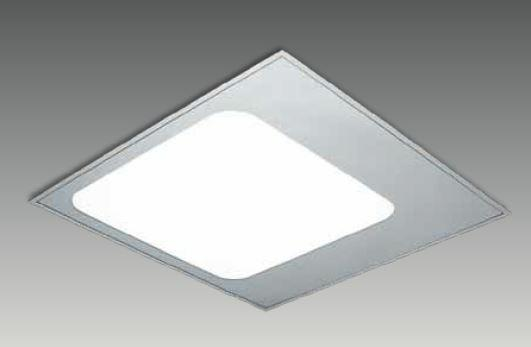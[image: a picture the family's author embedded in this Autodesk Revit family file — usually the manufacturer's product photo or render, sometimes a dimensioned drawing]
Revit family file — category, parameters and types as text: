
# Revit family: G 6060 RET
name_source: partatom
category: Lighting Fixtures
revit_build: Autodesk Revit 2017 (Build: 20160225_1515(x64)
units: mm (PartAtom-declared; Revit-internal decimal feet)

## family parameters
Always vertical = Yes
Cut with Voids When Loaded = No
Host = Ceiling
Light Source = Yes
OmniClass Number = 23.80.70.11
OmniClass Title = Luminaries for Internal Lighting
Part Type = Normal
Room Calculation Point = No
Round Connector Dimension = Use Diameter
Shared = No

## types (4) — shared parameters
Color Filter = 16777215
Dimming Lamp Color Temperature Shift = <None>
Emit Shape Visible in Rendering = Yes
Emit from Rectangle Length = 570 mm  [stored 1.87008 ft]
Emit from Rectangle Width = 570 mm  [stored 1.87008 ft]
Light Source Symbol Size = 610 mm
Manufacturer = ARLIGHT
Type Image = G 6060 RET.JPG

## per-type parameters (varying)
| type | Wattage Comments |
| GRET.6060.28.30 | 28 |
| GRET.6060.28.40 | 28 |
| GRET.6060.36.30 | 36W |
| GRET.6060.36.40 | 36W |

note: [stored X ft] marks values corroborated as IEEE doubles in the binary element streams (Revit-internal decimal feet)

## geometry (parser evidence)
native form markers: Sweep x2
no freeform markers — native parametric forms only
